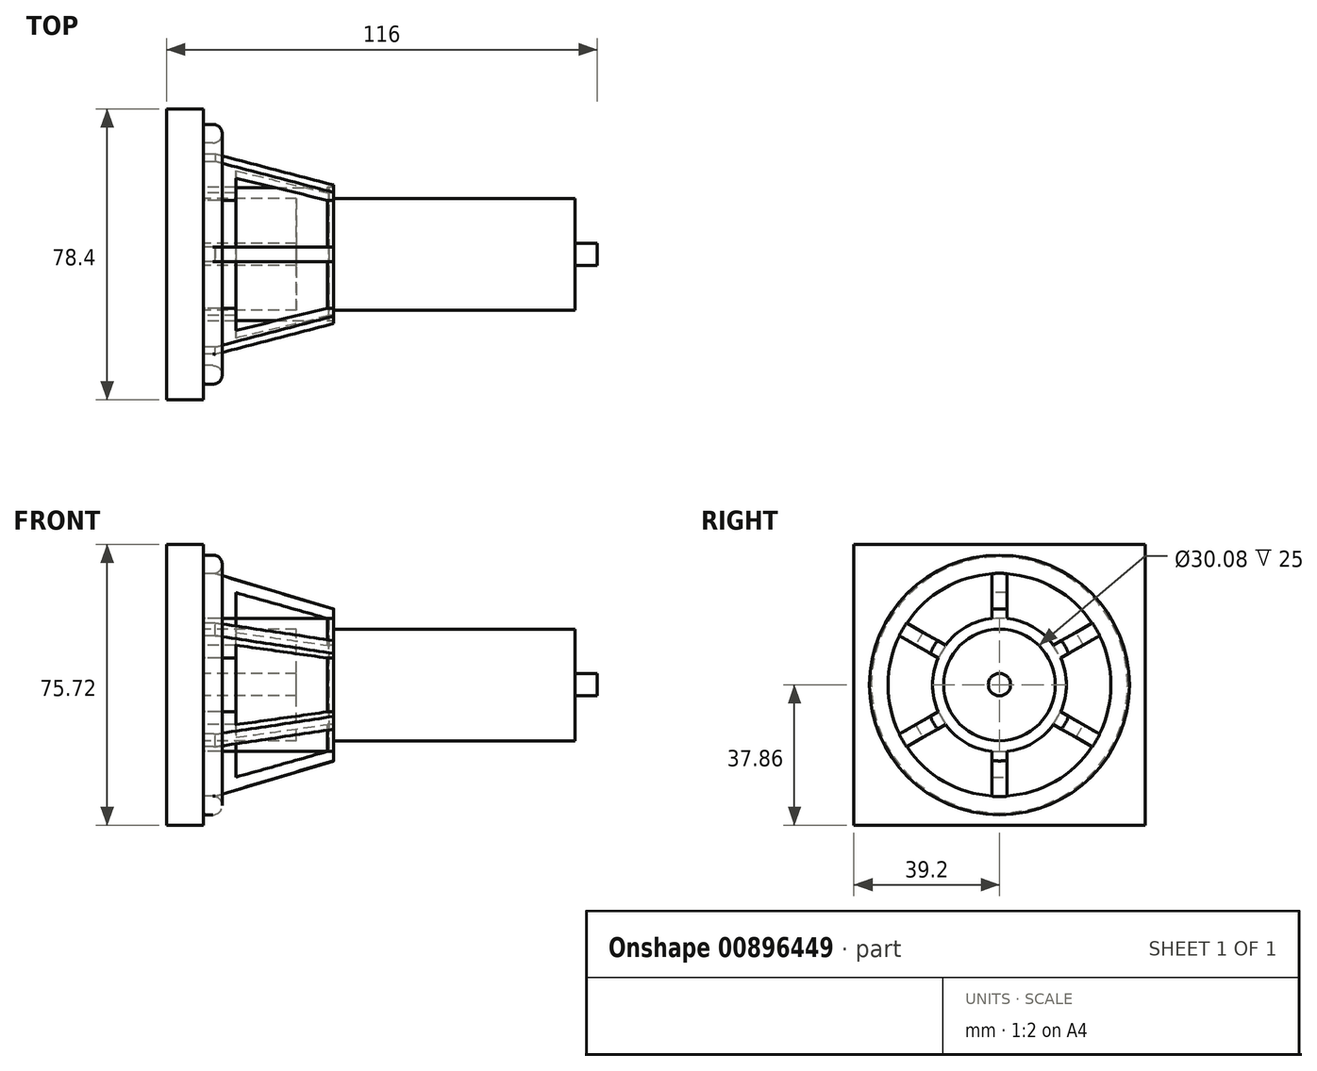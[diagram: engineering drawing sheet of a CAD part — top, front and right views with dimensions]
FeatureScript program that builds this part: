
annotation { "Feature Type Name" : "Feature", "Feature Type Description" : "" }
export const myFeature = defineFeature(function(context is Context, id is Id, definition is map)
    precondition{}
    {
        {
            var Q0;
            Q0=qCreatedBy(makeId("Right.planeOp"),FACE);
            var sketch = newSketch(context, id + "F0", { "sketchPlane" : qUnion([Q0])});
            skLineSegment(sketch, "E0.bottom", {"start": v(39.2, 37.86) * mm, "end": v(-39.2, 37.86) * mm});
            skLineSegment(sketch, "E0.top", {"start": v(39.2, -37.86) * mm, "end": v(-39.2, -37.86) * mm});
            skLineSegment(sketch, "E0.left", {"start": v(39.2, 37.86) * mm, "end": v(39.2, -37.86) * mm});
            skLineSegment(sketch, "E0.right", {"start": v(-39.2, 37.86) * mm, "end": v(-39.2, -37.86) * mm});
            skPoint(sketch, "E0.middle", {"position": v(0, 0) * mm});
            skSolve(sketch);
        }
        {
            var Q0;
            Q0=makeQuery(id+"F0.imprint","IMPRINT",FACE,{"disambiguationData":[TD([[makeQuery(id+"F0.imprint","IMPRINT",EDGE,{"derivedFrom":sQuery(id+"F0.wireOp",EDGE,"E0.bottom")}),1.0]])]});
            extrude(context, id + "F1", {"entities" : qUnion([Q0]), "oppositeDirection" : true, "depth" : 10 * mm, "offsetDistance" : 25 * mm});
        }
        {
            var Q0;
            Q0=makeQuery(id+"F1.opExtrude","CAP_FACE",FACE,{"disambiguationData":[OSD([sQuery(id+"F0.wireOp",EDGE,"E0.bottom"),sQuery(id+"F0.wireOp",EDGE,"E0.top"),sQuery(id+"F0.wireOp",EDGE,"E0.left"),sQuery(id+"F0.wireOp",EDGE,"E0.right")])],"isStart":true});
            var sketch = newSketch(context, id + "F2", { "sketchPlane" : qUnion([Q0])});
            skCircle(sketch, "E1", {"center": v(0, 0.06) * mm, "radius": 3 * mm});
            skSolve(sketch);
        }
        {
            var Q0;
            Q0 = qSketchRegion(id + "F2", true);
            extrude(context, id + "F3", {"entities" : qUnion([Q0]), "operationType" : NewBodyOperationType.ADD, "depth" : 6 * mm, "offsetDistance" : 25 * mm});
        }
        {
            var Q0;
            Q0=makeQuery(id+"F1.opExtrude","CAP_FACE",FACE,{"disambiguationData":[OSD([sQuery(id+"F0.wireOp",EDGE,"E0.bottom"),sQuery(id+"F0.wireOp",EDGE,"E0.top"),sQuery(id+"F0.wireOp",EDGE,"E0.left"),sQuery(id+"F0.wireOp",EDGE,"E0.right")])],"isStart":true});
            var sketch = newSketch(context, id + "F4", { "sketchPlane" : qUnion([Q0])});
            skCircle(sketch, "E2", {"center": v(0, 0) * mm, "radius": 15.04 * mm});
            skSolve(sketch);
        }
        {
            var Q0;
            Q0=makeQuery(id+"F4.imprint","IMPRINT",FACE,{"disambiguationData":[TD([[makeQuery(id+"F4.imprint","IMPRINT",EDGE,{"derivedFrom":sQuery(id+"F4.wireOp",EDGE,"E2")}),1.0]])]});
            var Q1;
            Q1=makeQuery(id+"F3.opExtrude","CAP_FACE",FACE,{"disambiguationData":[OSD([sQuery(id+"F2.wireOp",EDGE,"E1")])],"isStart":false});
            extrude(context, id + "F5", {"entities" : qUnion([Q0, Q1]), "depth" : 100 * mm, "offsetDistance" : 25 * mm});
        }
        {
            var Q0;
            Q0=qCreatedBy(makeId("Right.planeOp"),FACE);
            var sketch = newSketch(context, id + "F6", { "sketchPlane" : qUnion([Q0])});
            skCircle(sketch, "E3", {"center": v(0, 0) * mm, "radius": 35 * mm});
            skArc(sketch, "E4", {"start": v(14.54, 10.68) * mm, "mid": v(9.02, 15.62) * mm, "end": v(1.98, 17.93) * mm});
            skArc(sketch, "E5", {"start": v(24.93, 16.68) * mm, "mid": v(15, 25.98) * mm, "end": v(1.98, 29.93) * mm});
            skLineSegment(sketch, "E6", {"start": v(1.98, 29.93) * mm, "end": v(1.98, 17.93) * mm});
            skLineSegment(sketch, "E7", {"start": v(14.54, 10.68) * mm, "end": v(24.93, 16.68) * mm});
            skLineSegment(sketch, "E8.1.0", {"start": v(-1.98, 17.93) * mm, "end": v(-1.98, 29.93) * mm});
            skLineSegment(sketch, "E8.1.1", {"start": v(-24.93, 16.68) * mm, "end": v(-14.54, 10.68) * mm});
            skArc(sketch, "E8.1.2", {"start": v(-1.98, 29.93) * mm, "mid": v(-15, 25.98) * mm, "end": v(-24.93, 16.68) * mm});
            skArc(sketch, "E8.1.3", {"start": v(-1.98, 17.93) * mm, "mid": v(-9.02, 15.62) * mm, "end": v(-14.54, 10.68) * mm});
            skLineSegment(sketch, "E8.2.0", {"start": v(-16.52, 7.25) * mm, "end": v(-26.91, 13.25) * mm});
            skLineSegment(sketch, "E8.2.1", {"start": v(-26.91, -13.25) * mm, "end": v(-16.52, -7.25) * mm});
            skArc(sketch, "E8.2.2", {"start": v(-26.91, 13.25) * mm, "mid": v(-30, 0) * mm, "end": v(-26.91, -13.25) * mm});
            skArc(sketch, "E8.2.3", {"start": v(-16.52, 7.25) * mm, "mid": v(-18.04, 0) * mm, "end": v(-16.52, -7.25) * mm});
            skLineSegment(sketch, "E8.3.0", {"start": v(-14.54, -10.68) * mm, "end": v(-24.93, -16.68) * mm});
            skLineSegment(sketch, "E8.3.1", {"start": v(-1.98, -29.93) * mm, "end": v(-1.98, -17.93) * mm});
            skArc(sketch, "E8.3.2", {"start": v(-24.93, -16.68) * mm, "mid": v(-15, -25.98) * mm, "end": v(-1.98, -29.93) * mm});
            skArc(sketch, "E8.3.3", {"start": v(-14.54, -10.68) * mm, "mid": v(-9.02, -15.62) * mm, "end": v(-1.98, -17.93) * mm});
            skLineSegment(sketch, "E8.4.0", {"start": v(1.98, -17.93) * mm, "end": v(1.98, -29.93) * mm});
            skLineSegment(sketch, "E8.4.1", {"start": v(24.93, -16.68) * mm, "end": v(14.54, -10.68) * mm});
            skArc(sketch, "E8.4.2", {"start": v(1.98, -29.93) * mm, "mid": v(15, -25.98) * mm, "end": v(24.93, -16.68) * mm});
            skArc(sketch, "E8.4.3", {"start": v(1.98, -17.93) * mm, "mid": v(9.02, -15.62) * mm, "end": v(14.54, -10.68) * mm});
            skLineSegment(sketch, "E8.5.0", {"start": v(16.52, -7.25) * mm, "end": v(26.91, -13.25) * mm});
            skLineSegment(sketch, "E8.5.1", {"start": v(26.91, 13.25) * mm, "end": v(16.52, 7.25) * mm});
            skArc(sketch, "E8.5.2", {"start": v(26.91, -13.25) * mm, "mid": v(30, 0) * mm, "end": v(26.91, 13.25) * mm});
            skArc(sketch, "E8.5.3", {"start": v(16.52, -7.25) * mm, "mid": v(18.04, 0) * mm, "end": v(16.52, 7.25) * mm});
            skSolve(sketch);
        }
        {
            var Q0;
            Q0=makeQuery(id+"F6.imprint","IMPRINT",FACE,{"disambiguationData":[TD([[makeQuery(id+"F6.imprint","IMPRINT",EDGE,{"derivedFrom":sQuery(id+"F6.wireOp",EDGE,"E3")}),1.0]])]});
            extrude(context, id + "F7", {"entities" : qUnion([Q0]), "depth" : 5 * mm, "offsetDistance" : 25 * mm});
        }
        {
            var Q0;
            Q0=makeQuery(id+"F7.opExtrude","CAP_EDGE",EDGE,{"disambiguationData":[OSD([sQuery(id+"F6.wireOp",EDGE,"E3")])],"isStart":false});
            var Q1;
            Q1=makeQuery(id+"F7.opExtrude","CAP_EDGE",EDGE,{"disambiguationData":[OSD([sQuery(id+"F6.wireOp",EDGE,"E8.2.2")])],"isStart":false});
            var Q2;
            Q2=makeQuery(id+"F7.opExtrude","CAP_EDGE",EDGE,{"disambiguationData":[OSD([sQuery(id+"F6.wireOp",EDGE,"E8.1.2")])],"isStart":false});
            var Q3;
            Q3=makeQuery(id+"F7.opExtrude","CAP_EDGE",EDGE,{"disambiguationData":[OSD([sQuery(id+"F6.wireOp",EDGE,"E5")])],"isStart":false});
            var Q4;
            Q4=makeQuery(id+"F7.opExtrude","CAP_EDGE",EDGE,{"disambiguationData":[OSD([sQuery(id+"F6.wireOp",EDGE,"E8.4.2")])],"isStart":false});
            var Q5;
            Q5=makeQuery(id+"F7.opExtrude","CAP_EDGE",EDGE,{"disambiguationData":[OSD([sQuery(id+"F6.wireOp",EDGE,"E8.3.2")])],"isStart":false});
            var Q6;
            Q6=makeQuery(id+"F7.opExtrude","CAP_EDGE",EDGE,{"disambiguationData":[OSD([sQuery(id+"F6.wireOp",EDGE,"E8.5.2")])],"isStart":false});
            fillet(context, id + "F8", {"entities" : qUnion([Q0, Q1, Q2, Q3, Q4, Q5, Q6]), "radius" : 2.5 * mm, "tangentPropagation" : true, "allowEdgeOverflow" : false});
        }
        {
            var Q0;
            Q0=makeQuery(id+"F7.opExtrude","CAP_EDGE",EDGE,{"disambiguationData":[OSD([sQuery(id+"F6.wireOp",EDGE,"E3")])],"isStart":true});
            fillet(context, id + "F9", {"entities" : qUnion([Q0]), "radius" : 0.5 * mm, "tangentPropagation" : true, "allowEdgeOverflow" : false});
        }
        {
            var Q0;
            Q0=makeQuery(id+"F4.imprint","IMPRINT",FACE,{"disambiguationData":[TD([[makeQuery(id+"F4.imprint","IMPRINT",EDGE,{"derivedFrom":sQuery(id+"F4.wireOp",EDGE,"E2")}),1.0]])]});
            var Q1;
            Q1=makeQuery(id+"F4.imprint","IMPRINT",FACE,{"disambiguationData":[TD([[makeQuery(id+"F4.imprint","IMPRINT",EDGE,{"derivedFrom":makeQuery(id+"F3.opExtrude","CAP_EDGE",EDGE,{"disambiguationData":[OSD([sQuery(id+"F2.wireOp",EDGE,"E1")])],"isStart":true})}),1.0]])]});
            var Q2;
            Q2=sQuery(id+"F4.wireOp",EDGE,"E2");
            extrude(context, id + "F10", {"entities" : qUnion([Q0, Q1]), "operationType" : NewBodyOperationType.REMOVE, "surfaceEntities" : qUnion([Q2]), "depth" : 25 * mm, "offsetDistance" : 25 * mm});
        }
        {
            var Q0;
            Q0=makeQuery(id+"F7.opExtrude","CAP_FACE",FACE,{"disambiguationData":[OSD([sQuery(id+"F6.wireOp",EDGE,"E3"),sQuery(id+"F6.wireOp",EDGE,"E4"),sQuery(id+"F6.wireOp",EDGE,"E5"),sQuery(id+"F6.wireOp",EDGE,"E6"),sQuery(id+"F6.wireOp",EDGE,"E7"),sQuery(id+"F6.wireOp",EDGE,"E8.1.0"),sQuery(id+"F6.wireOp",EDGE,"E8.1.1"),sQuery(id+"F6.wireOp",EDGE,"E8.1.2"),sQuery(id+"F6.wireOp",EDGE,"E8.1.3"),sQuery(id+"F6.wireOp",EDGE,"E8.2.0"),sQuery(id+"F6.wireOp",EDGE,"E8.2.1"),sQuery(id+"F6.wireOp",EDGE,"E8.2.2"),sQuery(id+"F6.wireOp",EDGE,"E8.2.3"),sQuery(id+"F6.wireOp",EDGE,"E8.3.0"),sQuery(id+"F6.wireOp",EDGE,"E8.3.1"),sQuery(id+"F6.wireOp",EDGE,"E8.3.2"),sQuery(id+"F6.wireOp",EDGE,"E8.3.3"),sQuery(id+"F6.wireOp",EDGE,"E8.4.0"),sQuery(id+"F6.wireOp",EDGE,"E8.4.1"),sQuery(id+"F6.wireOp",EDGE,"E8.4.2"),sQuery(id+"F6.wireOp",EDGE,"E8.4.3"),sQuery(id+"F6.wireOp",EDGE,"E8.5.0"),sQuery(id+"F6.wireOp",EDGE,"E8.5.1"),sQuery(id+"F6.wireOp",EDGE,"E8.5.2"),sQuery(id+"F6.wireOp",EDGE,"E8.5.3")])],"isStart":false});
            extrude(context, id + "F11", {"entities" : qUnion([Q0]), "operationType" : NewBodyOperationType.ADD, "depth" : 30 * mm, "offsetDistance" : 25 * mm});
        }
        {
            var Q0;
            {var subQ0=sQuery(id+"F6.wireOp",EDGE,"E8.5.3");var subQ1=sQuery(id+"F6.wireOp",EDGE,"E8.5.2");var subQ2=sQuery(id+"F6.wireOp",EDGE,"E8.5.1");var subQ3=sQuery(id+"F6.wireOp",EDGE,"E8.5.0");var subQ4=sQuery(id+"F6.wireOp",EDGE,"E8.4.3");var subQ5=sQuery(id+"F6.wireOp",EDGE,"E8.4.2");var subQ6=sQuery(id+"F6.wireOp",EDGE,"E8.4.1");var subQ7=sQuery(id+"F6.wireOp",EDGE,"E8.4.0");var subQ8=sQuery(id+"F6.wireOp",EDGE,"E8.3.3");var subQ9=sQuery(id+"F6.wireOp",EDGE,"E8.3.2");var subQ10=sQuery(id+"F6.wireOp",EDGE,"E8.3.1");var subQ11=sQuery(id+"F6.wireOp",EDGE,"E8.3.0");var subQ12=sQuery(id+"F6.wireOp",EDGE,"E8.2.3");var subQ13=sQuery(id+"F6.wireOp",EDGE,"E8.2.2");var subQ14=sQuery(id+"F6.wireOp",EDGE,"E8.2.1");var subQ15=sQuery(id+"F6.wireOp",EDGE,"E8.2.0");var subQ16=sQuery(id+"F6.wireOp",EDGE,"E8.1.3");var subQ17=sQuery(id+"F6.wireOp",EDGE,"E8.1.2");var subQ18=sQuery(id+"F6.wireOp",EDGE,"E8.1.1");var subQ19=sQuery(id+"F6.wireOp",EDGE,"E8.1.0");var subQ20=sQuery(id+"F6.wireOp",EDGE,"E7");var subQ21=sQuery(id+"F6.wireOp",EDGE,"E6");var subQ22=sQuery(id+"F6.wireOp",EDGE,"E5");var subQ23=sQuery(id+"F6.wireOp",EDGE,"E4");var subQ24=sQuery(id+"F6.wireOp",EDGE,"E3");Q0=makeQuery(id+"F11.opExtrude","CAP_EDGE",EDGE,{"disambiguationData":[OSD([subQ24,subQ23,subQ22,subQ21,subQ20,subQ19,subQ18,subQ17,subQ16,subQ15,subQ14,subQ13,subQ12,subQ11,subQ10,subQ9,subQ8,subQ7,subQ6,subQ5,subQ4,subQ3,subQ2,subQ1,subQ0]),TDD([makeQuery(id+"F8.opFillet","BLEND_EDGE",EDGE,{"disambiguationData":[OD(3.0)],"blendedFrom":[makeQuery(id+"F7.opExtrude","CAP_EDGE",EDGE,{"disambiguationData":[OSD([subQ24])],"isStart":false}),makeQuery(id+"F7.opExtrude","CAP_FACE",FACE,{"disambiguationData":[OSD([subQ24,subQ23,subQ22,subQ21,subQ20,subQ19,subQ18,subQ17,subQ16,subQ15,subQ14,subQ13,subQ12,subQ11,subQ10,subQ9,subQ8,subQ7,subQ6,subQ5,subQ4,subQ3,subQ2,subQ1,subQ0])],"isStart":false})],"blendedInto":[makeQuery(id+"F7.opExtrude","CAP_FACE",FACE,{"disambiguationData":[OSD([subQ24,subQ23,subQ22,subQ21,subQ20,subQ19,subQ18,subQ17,subQ16,subQ15,subQ14,subQ13,subQ12,subQ11,subQ10,subQ9,subQ8,subQ7,subQ6,subQ5,subQ4,subQ3,subQ2,subQ1,subQ0])],"isStart":false})]})])],"isStart":false});}
            var Q1;
            {var subQ0=sQuery(id+"F6.wireOp",EDGE,"E8.5.3");var subQ1=sQuery(id+"F6.wireOp",EDGE,"E8.5.2");var subQ2=sQuery(id+"F6.wireOp",EDGE,"E8.5.1");var subQ3=sQuery(id+"F6.wireOp",EDGE,"E8.5.0");var subQ4=sQuery(id+"F6.wireOp",EDGE,"E8.4.3");var subQ5=sQuery(id+"F6.wireOp",EDGE,"E8.4.2");var subQ6=sQuery(id+"F6.wireOp",EDGE,"E8.4.1");var subQ7=sQuery(id+"F6.wireOp",EDGE,"E8.4.0");var subQ8=sQuery(id+"F6.wireOp",EDGE,"E8.3.3");var subQ9=sQuery(id+"F6.wireOp",EDGE,"E8.3.2");var subQ10=sQuery(id+"F6.wireOp",EDGE,"E8.3.1");var subQ11=sQuery(id+"F6.wireOp",EDGE,"E8.3.0");var subQ12=sQuery(id+"F6.wireOp",EDGE,"E8.2.3");var subQ13=sQuery(id+"F6.wireOp",EDGE,"E8.2.2");var subQ14=sQuery(id+"F6.wireOp",EDGE,"E8.2.1");var subQ15=sQuery(id+"F6.wireOp",EDGE,"E8.2.0");var subQ16=sQuery(id+"F6.wireOp",EDGE,"E8.1.3");var subQ17=sQuery(id+"F6.wireOp",EDGE,"E8.1.2");var subQ18=sQuery(id+"F6.wireOp",EDGE,"E8.1.1");var subQ19=sQuery(id+"F6.wireOp",EDGE,"E8.1.0");var subQ20=sQuery(id+"F6.wireOp",EDGE,"E7");var subQ21=sQuery(id+"F6.wireOp",EDGE,"E6");var subQ22=sQuery(id+"F6.wireOp",EDGE,"E5");var subQ23=sQuery(id+"F6.wireOp",EDGE,"E4");var subQ24=sQuery(id+"F6.wireOp",EDGE,"E3");Q1=makeQuery(id+"F11.opExtrude","CAP_EDGE",EDGE,{"disambiguationData":[OSD([subQ24,subQ23,subQ22,subQ21,subQ20,subQ19,subQ18,subQ17,subQ16,subQ15,subQ14,subQ13,subQ12,subQ11,subQ10,subQ9,subQ8,subQ7,subQ6,subQ5,subQ4,subQ3,subQ2,subQ1,subQ0]),TDD([makeQuery(id+"F8.opFillet","BLEND_EDGE",EDGE,{"disambiguationData":[OD(2.0)],"blendedFrom":[makeQuery(id+"F7.opExtrude","CAP_EDGE",EDGE,{"disambiguationData":[OSD([subQ24])],"isStart":false}),makeQuery(id+"F7.opExtrude","CAP_FACE",FACE,{"disambiguationData":[OSD([subQ24,subQ23,subQ22,subQ21,subQ20,subQ19,subQ18,subQ17,subQ16,subQ15,subQ14,subQ13,subQ12,subQ11,subQ10,subQ9,subQ8,subQ7,subQ6,subQ5,subQ4,subQ3,subQ2,subQ1,subQ0])],"isStart":false})],"blendedInto":[makeQuery(id+"F7.opExtrude","CAP_FACE",FACE,{"disambiguationData":[OSD([subQ24,subQ23,subQ22,subQ21,subQ20,subQ19,subQ18,subQ17,subQ16,subQ15,subQ14,subQ13,subQ12,subQ11,subQ10,subQ9,subQ8,subQ7,subQ6,subQ5,subQ4,subQ3,subQ2,subQ1,subQ0])],"isStart":false})]})])],"isStart":false});}
            var Q2;
            {var subQ0=sQuery(id+"F6.wireOp",EDGE,"E8.5.3");var subQ1=sQuery(id+"F6.wireOp",EDGE,"E8.5.2");var subQ2=sQuery(id+"F6.wireOp",EDGE,"E8.5.1");var subQ3=sQuery(id+"F6.wireOp",EDGE,"E8.5.0");var subQ4=sQuery(id+"F6.wireOp",EDGE,"E8.4.3");var subQ5=sQuery(id+"F6.wireOp",EDGE,"E8.4.2");var subQ6=sQuery(id+"F6.wireOp",EDGE,"E8.4.1");var subQ7=sQuery(id+"F6.wireOp",EDGE,"E8.4.0");var subQ8=sQuery(id+"F6.wireOp",EDGE,"E8.3.3");var subQ9=sQuery(id+"F6.wireOp",EDGE,"E8.3.2");var subQ10=sQuery(id+"F6.wireOp",EDGE,"E8.3.1");var subQ11=sQuery(id+"F6.wireOp",EDGE,"E8.3.0");var subQ12=sQuery(id+"F6.wireOp",EDGE,"E8.2.3");var subQ13=sQuery(id+"F6.wireOp",EDGE,"E8.2.2");var subQ14=sQuery(id+"F6.wireOp",EDGE,"E8.2.1");var subQ15=sQuery(id+"F6.wireOp",EDGE,"E8.2.0");var subQ16=sQuery(id+"F6.wireOp",EDGE,"E8.1.3");var subQ17=sQuery(id+"F6.wireOp",EDGE,"E8.1.2");var subQ18=sQuery(id+"F6.wireOp",EDGE,"E8.1.1");var subQ19=sQuery(id+"F6.wireOp",EDGE,"E8.1.0");var subQ20=sQuery(id+"F6.wireOp",EDGE,"E7");var subQ21=sQuery(id+"F6.wireOp",EDGE,"E6");var subQ22=sQuery(id+"F6.wireOp",EDGE,"E5");var subQ23=sQuery(id+"F6.wireOp",EDGE,"E4");var subQ24=sQuery(id+"F6.wireOp",EDGE,"E3");Q2=makeQuery(id+"F11.opExtrude","CAP_EDGE",EDGE,{"disambiguationData":[OSD([subQ24,subQ23,subQ22,subQ21,subQ20,subQ19,subQ18,subQ17,subQ16,subQ15,subQ14,subQ13,subQ12,subQ11,subQ10,subQ9,subQ8,subQ7,subQ6,subQ5,subQ4,subQ3,subQ2,subQ1,subQ0]),TDD([makeQuery(id+"F8.opFillet","BLEND_EDGE",EDGE,{"disambiguationData":[OD(4.0)],"blendedFrom":[makeQuery(id+"F7.opExtrude","CAP_EDGE",EDGE,{"disambiguationData":[OSD([subQ24])],"isStart":false}),makeQuery(id+"F7.opExtrude","CAP_FACE",FACE,{"disambiguationData":[OSD([subQ24,subQ23,subQ22,subQ21,subQ20,subQ19,subQ18,subQ17,subQ16,subQ15,subQ14,subQ13,subQ12,subQ11,subQ10,subQ9,subQ8,subQ7,subQ6,subQ5,subQ4,subQ3,subQ2,subQ1,subQ0])],"isStart":false})],"blendedInto":[makeQuery(id+"F7.opExtrude","CAP_FACE",FACE,{"disambiguationData":[OSD([subQ24,subQ23,subQ22,subQ21,subQ20,subQ19,subQ18,subQ17,subQ16,subQ15,subQ14,subQ13,subQ12,subQ11,subQ10,subQ9,subQ8,subQ7,subQ6,subQ5,subQ4,subQ3,subQ2,subQ1,subQ0])],"isStart":false})]})])],"isStart":false});}
            var Q3;
            {var subQ0=sQuery(id+"F6.wireOp",EDGE,"E8.5.3");var subQ1=sQuery(id+"F6.wireOp",EDGE,"E8.5.2");var subQ2=sQuery(id+"F6.wireOp",EDGE,"E8.5.1");var subQ3=sQuery(id+"F6.wireOp",EDGE,"E8.5.0");var subQ4=sQuery(id+"F6.wireOp",EDGE,"E8.4.3");var subQ5=sQuery(id+"F6.wireOp",EDGE,"E8.4.2");var subQ6=sQuery(id+"F6.wireOp",EDGE,"E8.4.1");var subQ7=sQuery(id+"F6.wireOp",EDGE,"E8.4.0");var subQ8=sQuery(id+"F6.wireOp",EDGE,"E8.3.3");var subQ9=sQuery(id+"F6.wireOp",EDGE,"E8.3.2");var subQ10=sQuery(id+"F6.wireOp",EDGE,"E8.3.1");var subQ11=sQuery(id+"F6.wireOp",EDGE,"E8.3.0");var subQ12=sQuery(id+"F6.wireOp",EDGE,"E8.2.3");var subQ13=sQuery(id+"F6.wireOp",EDGE,"E8.2.2");var subQ14=sQuery(id+"F6.wireOp",EDGE,"E8.2.1");var subQ15=sQuery(id+"F6.wireOp",EDGE,"E8.2.0");var subQ16=sQuery(id+"F6.wireOp",EDGE,"E8.1.3");var subQ17=sQuery(id+"F6.wireOp",EDGE,"E8.1.2");var subQ18=sQuery(id+"F6.wireOp",EDGE,"E8.1.1");var subQ19=sQuery(id+"F6.wireOp",EDGE,"E8.1.0");var subQ20=sQuery(id+"F6.wireOp",EDGE,"E7");var subQ21=sQuery(id+"F6.wireOp",EDGE,"E6");var subQ22=sQuery(id+"F6.wireOp",EDGE,"E5");var subQ23=sQuery(id+"F6.wireOp",EDGE,"E4");var subQ24=sQuery(id+"F6.wireOp",EDGE,"E3");Q3=makeQuery(id+"F11.opExtrude","CAP_EDGE",EDGE,{"disambiguationData":[OSD([subQ24,subQ23,subQ22,subQ21,subQ20,subQ19,subQ18,subQ17,subQ16,subQ15,subQ14,subQ13,subQ12,subQ11,subQ10,subQ9,subQ8,subQ7,subQ6,subQ5,subQ4,subQ3,subQ2,subQ1,subQ0]),TDD([makeQuery(id+"F8.opFillet","BLEND_EDGE",EDGE,{"disambiguationData":[OD(5.0)],"blendedFrom":[makeQuery(id+"F7.opExtrude","CAP_EDGE",EDGE,{"disambiguationData":[OSD([subQ24])],"isStart":false}),makeQuery(id+"F7.opExtrude","CAP_FACE",FACE,{"disambiguationData":[OSD([subQ24,subQ23,subQ22,subQ21,subQ20,subQ19,subQ18,subQ17,subQ16,subQ15,subQ14,subQ13,subQ12,subQ11,subQ10,subQ9,subQ8,subQ7,subQ6,subQ5,subQ4,subQ3,subQ2,subQ1,subQ0])],"isStart":false})],"blendedInto":[makeQuery(id+"F7.opExtrude","CAP_FACE",FACE,{"disambiguationData":[OSD([subQ24,subQ23,subQ22,subQ21,subQ20,subQ19,subQ18,subQ17,subQ16,subQ15,subQ14,subQ13,subQ12,subQ11,subQ10,subQ9,subQ8,subQ7,subQ6,subQ5,subQ4,subQ3,subQ2,subQ1,subQ0])],"isStart":false})]})])],"isStart":false});}
            var Q4;
            {var subQ0=sQuery(id+"F6.wireOp",EDGE,"E8.5.3");var subQ1=sQuery(id+"F6.wireOp",EDGE,"E8.5.2");var subQ2=sQuery(id+"F6.wireOp",EDGE,"E8.5.1");var subQ3=sQuery(id+"F6.wireOp",EDGE,"E8.5.0");var subQ4=sQuery(id+"F6.wireOp",EDGE,"E8.4.3");var subQ5=sQuery(id+"F6.wireOp",EDGE,"E8.4.2");var subQ6=sQuery(id+"F6.wireOp",EDGE,"E8.4.1");var subQ7=sQuery(id+"F6.wireOp",EDGE,"E8.4.0");var subQ8=sQuery(id+"F6.wireOp",EDGE,"E8.3.3");var subQ9=sQuery(id+"F6.wireOp",EDGE,"E8.3.2");var subQ10=sQuery(id+"F6.wireOp",EDGE,"E8.3.1");var subQ11=sQuery(id+"F6.wireOp",EDGE,"E8.3.0");var subQ12=sQuery(id+"F6.wireOp",EDGE,"E8.2.3");var subQ13=sQuery(id+"F6.wireOp",EDGE,"E8.2.2");var subQ14=sQuery(id+"F6.wireOp",EDGE,"E8.2.1");var subQ15=sQuery(id+"F6.wireOp",EDGE,"E8.2.0");var subQ16=sQuery(id+"F6.wireOp",EDGE,"E8.1.3");var subQ17=sQuery(id+"F6.wireOp",EDGE,"E8.1.2");var subQ18=sQuery(id+"F6.wireOp",EDGE,"E8.1.1");var subQ19=sQuery(id+"F6.wireOp",EDGE,"E8.1.0");var subQ20=sQuery(id+"F6.wireOp",EDGE,"E7");var subQ21=sQuery(id+"F6.wireOp",EDGE,"E6");var subQ22=sQuery(id+"F6.wireOp",EDGE,"E5");var subQ23=sQuery(id+"F6.wireOp",EDGE,"E4");var subQ24=sQuery(id+"F6.wireOp",EDGE,"E3");Q4=makeQuery(id+"F11.opExtrude","CAP_EDGE",EDGE,{"disambiguationData":[OSD([subQ24,subQ23,subQ22,subQ21,subQ20,subQ19,subQ18,subQ17,subQ16,subQ15,subQ14,subQ13,subQ12,subQ11,subQ10,subQ9,subQ8,subQ7,subQ6,subQ5,subQ4,subQ3,subQ2,subQ1,subQ0]),TDD([makeQuery(id+"F8.opFillet","BLEND_EDGE",EDGE,{"disambiguationData":[OD(1.0)],"blendedFrom":[makeQuery(id+"F7.opExtrude","CAP_EDGE",EDGE,{"disambiguationData":[OSD([subQ24])],"isStart":false}),makeQuery(id+"F7.opExtrude","CAP_FACE",FACE,{"disambiguationData":[OSD([subQ24,subQ23,subQ22,subQ21,subQ20,subQ19,subQ18,subQ17,subQ16,subQ15,subQ14,subQ13,subQ12,subQ11,subQ10,subQ9,subQ8,subQ7,subQ6,subQ5,subQ4,subQ3,subQ2,subQ1,subQ0])],"isStart":false})],"blendedInto":[makeQuery(id+"F7.opExtrude","CAP_FACE",FACE,{"disambiguationData":[OSD([subQ24,subQ23,subQ22,subQ21,subQ20,subQ19,subQ18,subQ17,subQ16,subQ15,subQ14,subQ13,subQ12,subQ11,subQ10,subQ9,subQ8,subQ7,subQ6,subQ5,subQ4,subQ3,subQ2,subQ1,subQ0])],"isStart":false})]})])],"isStart":false});}
            var Q5;
            {var subQ0=sQuery(id+"F6.wireOp",EDGE,"E8.5.3");var subQ1=sQuery(id+"F6.wireOp",EDGE,"E8.5.2");var subQ2=sQuery(id+"F6.wireOp",EDGE,"E8.5.1");var subQ3=sQuery(id+"F6.wireOp",EDGE,"E8.5.0");var subQ4=sQuery(id+"F6.wireOp",EDGE,"E8.4.3");var subQ5=sQuery(id+"F6.wireOp",EDGE,"E8.4.2");var subQ6=sQuery(id+"F6.wireOp",EDGE,"E8.4.1");var subQ7=sQuery(id+"F6.wireOp",EDGE,"E8.4.0");var subQ8=sQuery(id+"F6.wireOp",EDGE,"E8.3.3");var subQ9=sQuery(id+"F6.wireOp",EDGE,"E8.3.2");var subQ10=sQuery(id+"F6.wireOp",EDGE,"E8.3.1");var subQ11=sQuery(id+"F6.wireOp",EDGE,"E8.3.0");var subQ12=sQuery(id+"F6.wireOp",EDGE,"E8.2.3");var subQ13=sQuery(id+"F6.wireOp",EDGE,"E8.2.2");var subQ14=sQuery(id+"F6.wireOp",EDGE,"E8.2.1");var subQ15=sQuery(id+"F6.wireOp",EDGE,"E8.2.0");var subQ16=sQuery(id+"F6.wireOp",EDGE,"E8.1.3");var subQ17=sQuery(id+"F6.wireOp",EDGE,"E8.1.2");var subQ18=sQuery(id+"F6.wireOp",EDGE,"E8.1.1");var subQ19=sQuery(id+"F6.wireOp",EDGE,"E8.1.0");var subQ20=sQuery(id+"F6.wireOp",EDGE,"E7");var subQ21=sQuery(id+"F6.wireOp",EDGE,"E6");var subQ22=sQuery(id+"F6.wireOp",EDGE,"E5");var subQ23=sQuery(id+"F6.wireOp",EDGE,"E4");var subQ24=sQuery(id+"F6.wireOp",EDGE,"E3");Q5=makeQuery(id+"F11.opExtrude","CAP_EDGE",EDGE,{"disambiguationData":[OSD([subQ24,subQ23,subQ22,subQ21,subQ20,subQ19,subQ18,subQ17,subQ16,subQ15,subQ14,subQ13,subQ12,subQ11,subQ10,subQ9,subQ8,subQ7,subQ6,subQ5,subQ4,subQ3,subQ2,subQ1,subQ0]),TDD([makeQuery(id+"F8.opFillet","BLEND_EDGE",EDGE,{"disambiguationData":[OD(0.0)],"blendedFrom":[makeQuery(id+"F7.opExtrude","CAP_EDGE",EDGE,{"disambiguationData":[OSD([subQ24])],"isStart":false}),makeQuery(id+"F7.opExtrude","CAP_FACE",FACE,{"disambiguationData":[OSD([subQ24,subQ23,subQ22,subQ21,subQ20,subQ19,subQ18,subQ17,subQ16,subQ15,subQ14,subQ13,subQ12,subQ11,subQ10,subQ9,subQ8,subQ7,subQ6,subQ5,subQ4,subQ3,subQ2,subQ1,subQ0])],"isStart":false})],"blendedInto":[makeQuery(id+"F7.opExtrude","CAP_FACE",FACE,{"disambiguationData":[OSD([subQ24,subQ23,subQ22,subQ21,subQ20,subQ19,subQ18,subQ17,subQ16,subQ15,subQ14,subQ13,subQ12,subQ11,subQ10,subQ9,subQ8,subQ7,subQ6,subQ5,subQ4,subQ3,subQ2,subQ1,subQ0])],"isStart":false})]})])],"isStart":false});}
            chamfer(context, id + "F12", {"entities" : qUnion([Q0, Q1, Q2, Q3, Q4, Q5]), "chamferType" : ChamferType.TWO_OFFSETS, "width1" : 12 * mm, "oppositeDirection" : false, "width2" : 40 * mm, "tangentPropagation" : true});
        }
        {
            var Q0;
            Q0=qCreatedBy(makeId("Front.planeOp"),FACE);
            var sketch = newSketch(context, id + "F13", { "sketchPlane" : qUnion([Q0])});
            skLineSegment(sketch, "E9", {"start": v(8.7, 17.93) * mm, "end": v(8.7, 24.93) * mm});
            skLineSegment(sketch, "E10", {"start": v(8.7, 24.93) * mm, "end": v(33.7, 17.93) * mm});
            skLineSegment(sketch, "E11", {"start": v(33.7, 17.93) * mm, "end": v(8.7, 17.93) * mm});
            skLineSegment(sketch, "E12", {"start": v(-49.17, 0) * mm, "end": v(54.34, 0) * mm});
            skSolve(sketch);
        }
        {
            var Q0;
            Q0=makeQuery(id+"F13.imprint","IMPRINT",FACE,{"disambiguationData":[TD([[makeQuery(id+"F13.imprint","IMPRINT",EDGE,{"derivedFrom":sQuery(id+"F13.wireOp",EDGE,"E9")}),-1.0]])]});
            var Q1;
            Q1=sQuery(id+"F13.wireOp",EDGE,"E12");
            revolve(context, id + "F14", {"operationType" : NewBodyOperationType.REMOVE, "surfaceOperationType" : NewSurfaceOperationType.NEW, "entities" : qUnion([Q0]), "axis" : qUnion([Q1]), "revolveType" : RevolveType.FULL, "oppositeDirection" : true});
        }
    });
